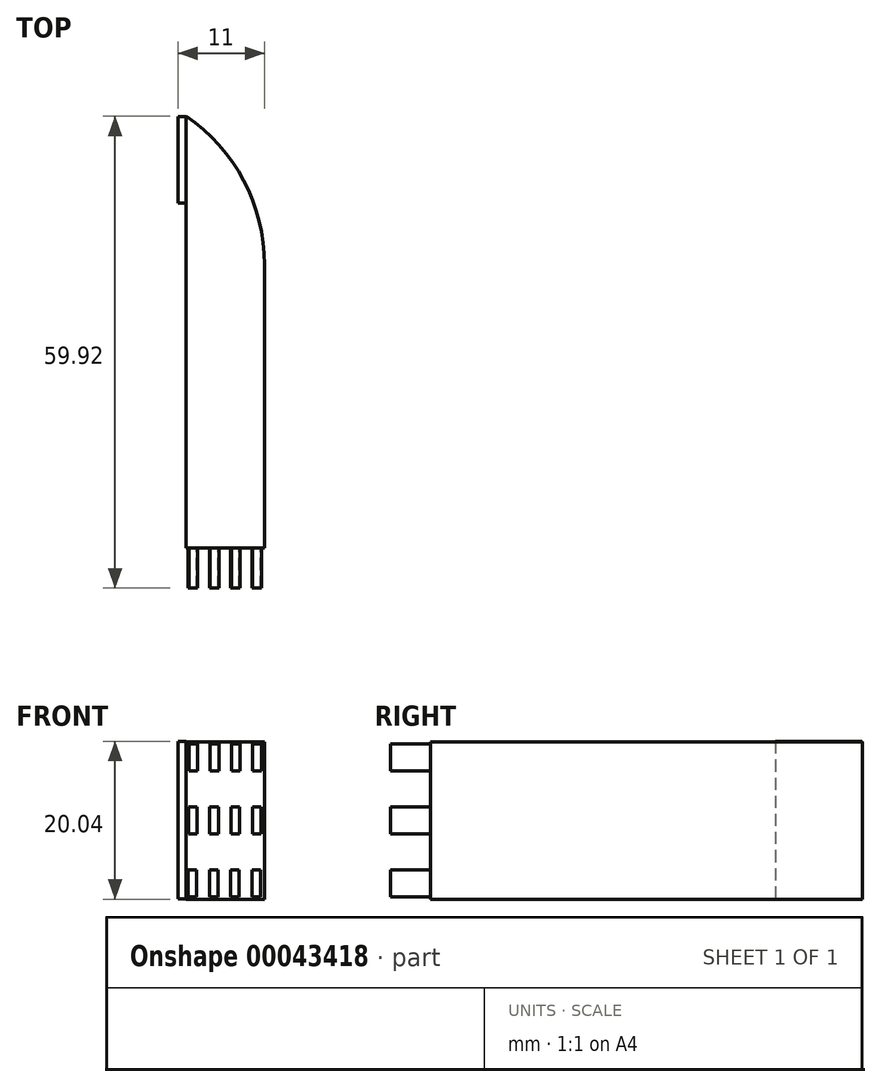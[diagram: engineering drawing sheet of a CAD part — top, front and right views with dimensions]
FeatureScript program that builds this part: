
annotation { "Feature Type Name" : "Feature", "Feature Type Description" : "" }
export const myFeature = defineFeature(function(context is Context, id is Id, definition is map)
    precondition{}
    {
        {
            var Q0;
            Q0=qCreatedBy(makeId("Front.planeOp"),FACE);
            var sketch = newSketch(context, id + "F0", { "sketchPlane" : qUnion([Q0])});
            skLineSegment(sketch, "E0.rect.bottom", {"start": v(-5, 10) * mm, "end": v(5, 10) * mm});
            skLineSegment(sketch, "E0.rect.top", {"start": v(-5, -10) * mm, "end": v(5, -10) * mm});
            skLineSegment(sketch, "E0.rect.left", {"start": v(-5, 10) * mm, "end": v(-5, -10) * mm});
            skLineSegment(sketch, "E0.rect.right", {"start": v(5, 10) * mm, "end": v(5, -10) * mm});
            skPoint(sketch, "E0.rect.middle", {"position": v(0, 0) * mm});
            skSolve(sketch);
        }
        {
            var Q0;
            Q0=qSketchRegion(id+"F0",true);
            extrude(context, id + "F1", {"entities" : qUnion([Q0]), "oppositeDirection" : true, "depth" : 25 * mm});
        }
        {
            var Q0;
            Q0=makeQuery(id+"F1.opExtrude","CAP_EDGE",EDGE,{"disambiguationData":[OSD([sQuery(id+"F0.wireOp",EDGE,"E0.rect.left")])],"isStart":false});
            cPlane(context, id + "F2", {"entities" : qUnion([Q0]), "cplaneType" : CPlaneType.LINE_ANGLE, "offset" : 150 * mm, "angle" : 0 * degree, "width" : 150 * mm, "height" : 150 * mm});
        }
        {
            var Q0;
            Q0=qCreatedBy(id+"F2.planeOp",FACE);
            var sketch = newSketch(context, id + "F3", { "sketchPlane" : qUnion([Q0])});
            skLineSegment(sketch, "E1.rect.bottom", {"start": v(-54.87, 10) * mm, "end": v(-24.87, 10) * mm});
            skLineSegment(sketch, "E1.rect.top", {"start": v(-54.87, -10) * mm, "end": v(-24.87, -10) * mm});
            skLineSegment(sketch, "E1.rect.left", {"start": v(-54.87, 10) * mm, "end": v(-54.87, -10) * mm});
            skLineSegment(sketch, "E1.rect.right", {"start": v(-24.87, 10) * mm, "end": v(-24.87, -10) * mm});
            skPoint(sketch, "E1.rect.middle", {"position": v(-39.87, 0) * mm});
            skSolve(sketch);
        }
        {
            var Q0;
            Q0=makeQuery(id+"F3.imprint","IMPRINT",FACE,{"disambiguationData":[TD([[makeQuery(id+"F3.imprint","IMPRINT",EDGE,{"derivedFrom":sQuery(id+"F3.wireOp",EDGE,"E1.rect.bottom")}),-1.0]])]});
            extrude(context, id + "F4", {"entities" : qUnion([Q0]), "operationType" : NewBodyOperationType.ADD, "oppositeDirection" : true, "depth" : 10 * mm});
        }
        {
            var Q0;
            Q0=makeQuery(id+"F4.opExtrude","CAP_EDGE",EDGE,{"disambiguationData":[OSD([sQuery(id+"F3.wireOp",EDGE,"E1.rect.left")])],"isStart":false});
            fillet(context, id + "F5", {"entities" : qUnion([Q0]), "radius" : 22.72 * mm, "tangentPropagation" : true, "allowEdgeOverflow" : false});
        }
        {
            var Q0;
            Q0=qCreatedBy(id+"F2.planeOp",FACE);
            var sketch = newSketch(context, id + "F6", { "sketchPlane" : qUnion([Q0])});
            skLineSegment(sketch, "E2.bottom", {"start": v(-54.82, 10.04) * mm, "end": v(-43.82, 10.04) * mm});
            skLineSegment(sketch, "E2.top", {"start": v(-54.82, -9.96) * mm, "end": v(-43.82, -9.96) * mm});
            skLineSegment(sketch, "E2.left", {"start": v(-54.82, 10.04) * mm, "end": v(-54.82, -9.96) * mm});
            skLineSegment(sketch, "E2.right", {"start": v(-43.82, 10.04) * mm, "end": v(-43.82, -9.96) * mm});
            skSolve(sketch);
        }
        {
            var Q0;
            Q0=makeQuery(id+"F6.imprint","IMPRINT",FACE,{"disambiguationData":[TD([[makeQuery(id+"F6.imprint","IMPRINT",EDGE,{"derivedFrom":sQuery(id+"F6.wireOp",EDGE,"E2.bottom")}),-1.0]])]});
            extrude(context, id + "F7", {"entities" : qUnion([Q0]), "operationType" : NewBodyOperationType.ADD, "depth" : 1 * mm});
        }
        {
            var Q0;
            Q0=makeQuery(id+"F1.opExtrude","CAP_FACE",FACE,{"disambiguationData":[OSD([sQuery(id+"F0.wireOp",EDGE,"E0.rect.bottom"),sQuery(id+"F0.wireOp",EDGE,"E0.rect.top"),sQuery(id+"F0.wireOp",EDGE,"E0.rect.left"),sQuery(id+"F0.wireOp",EDGE,"E0.rect.right")])],"isStart":true});
            var sketch = newSketch(context, id + "F8", { "sketchPlane" : qUnion([Q0])});
            skLineSegment(sketch, "E3.bottom", {"start": v(-4.6, 9.7) * mm, "end": v(-3.5, 9.7) * mm});
            skLineSegment(sketch, "E3.top", {"start": v(-4.6, 6.3) * mm, "end": v(-3.5, 6.3) * mm});
            skLineSegment(sketch, "E3.left", {"start": v(-4.6, 9.7) * mm, "end": v(-4.6, 6.3) * mm});
            skLineSegment(sketch, "E3.right", {"start": v(-3.5, 9.7) * mm, "end": v(-3.5, 6.3) * mm});
            skLineSegment(sketch, "E4.1.0.0", {"start": v(-0.8, 9.7) * mm, "end": v(-0.8, 6.3) * mm});
            skLineSegment(sketch, "E4.1.0.1", {"start": v(-1.9, 9.7) * mm, "end": v(-0.8, 9.7) * mm});
            skLineSegment(sketch, "E4.1.0.2", {"start": v(-1.9, 9.7) * mm, "end": v(-1.9, 6.3) * mm});
            skLineSegment(sketch, "E4.1.0.3", {"start": v(-1.9, 6.3) * mm, "end": v(-0.8, 6.3) * mm});
            skLineSegment(sketch, "E4.2.0.0", {"start": v(1.9, 9.7) * mm, "end": v(1.9, 6.3) * mm});
            skLineSegment(sketch, "E4.2.0.1", {"start": v(0.8, 9.7) * mm, "end": v(1.9, 9.7) * mm});
            skLineSegment(sketch, "E4.2.0.2", {"start": v(0.8, 9.7) * mm, "end": v(0.8, 6.3) * mm});
            skLineSegment(sketch, "E4.2.0.3", {"start": v(0.8, 6.3) * mm, "end": v(1.9, 6.3) * mm});
            skLineSegment(sketch, "E4.3.0.0", {"start": v(4.6, 9.7) * mm, "end": v(4.6, 6.3) * mm});
            skLineSegment(sketch, "E4.3.0.1", {"start": v(3.5, 9.7) * mm, "end": v(4.6, 9.7) * mm});
            skLineSegment(sketch, "E4.3.0.2", {"start": v(3.5, 9.7) * mm, "end": v(3.5, 6.3) * mm});
            skLineSegment(sketch, "E4.3.0.3", {"start": v(3.5, 6.3) * mm, "end": v(4.6, 6.3) * mm});
            skLineSegment(sketch, "E4.direction1", {"start": v(-3.5, 6.3) * mm, "end": v(-0.8, 6.3) * mm, "construction": true});
            skLineSegment(sketch, "E5.1.0.0", {"start": v(-4.66, -1.7) * mm, "end": v(-3.56, -1.7) * mm});
            skLineSegment(sketch, "E5.1.0.1", {"start": v(-4.66, 1.7) * mm, "end": v(-4.66, -1.7) * mm});
            skLineSegment(sketch, "E5.1.0.2", {"start": v(-3.56, 1.7) * mm, "end": v(-3.56, -1.7) * mm});
            skLineSegment(sketch, "E5.1.0.3", {"start": v(-4.66, 1.7) * mm, "end": v(-3.56, 1.7) * mm});
            skLineSegment(sketch, "E5.2.0.0", {"start": v(-4.72, -9.7) * mm, "end": v(-3.62, -9.7) * mm});
            skLineSegment(sketch, "E5.2.0.1", {"start": v(-4.72, -6.3) * mm, "end": v(-4.72, -9.7) * mm});
            skLineSegment(sketch, "E5.2.0.2", {"start": v(-3.62, -6.3) * mm, "end": v(-3.62, -9.7) * mm});
            skLineSegment(sketch, "E5.2.0.3", {"start": v(-4.72, -6.3) * mm, "end": v(-3.62, -6.3) * mm});
            skLineSegment(sketch, "E5.direction1", {"start": v(-4.6, 6.3) * mm, "end": v(-4.66, -1.7) * mm, "construction": true});
            skLineSegment(sketch, "E6.1.0.0", {"start": v(-1.96, 1.7) * mm, "end": v(-1.96, -1.7) * mm});
            skLineSegment(sketch, "E6.1.0.1", {"start": v(-1.96, -1.7) * mm, "end": v(-0.86, -1.7) * mm});
            skLineSegment(sketch, "E6.1.0.2", {"start": v(-0.86, 1.7) * mm, "end": v(-0.86, -1.7) * mm});
            skLineSegment(sketch, "E6.1.0.3", {"start": v(-1.96, 1.7) * mm, "end": v(-0.86, 1.7) * mm});
            skLineSegment(sketch, "E6.2.0.0", {"start": v(-2.02, -6.3) * mm, "end": v(-2.02, -9.7) * mm});
            skLineSegment(sketch, "E6.2.0.1", {"start": v(-2.02, -9.7) * mm, "end": v(-0.92, -9.7) * mm});
            skLineSegment(sketch, "E6.2.0.2", {"start": v(-0.92, -6.3) * mm, "end": v(-0.92, -9.7) * mm});
            skLineSegment(sketch, "E6.2.0.3", {"start": v(-2.02, -6.3) * mm, "end": v(-0.92, -6.3) * mm});
            skLineSegment(sketch, "E6.direction1", {"start": v(-1.9, 6.3) * mm, "end": v(-1.96, -1.7) * mm, "construction": true});
            skLineSegment(sketch, "E7.1.0.0", {"start": v(1.84, 1.7) * mm, "end": v(1.84, -1.7) * mm});
            skLineSegment(sketch, "E7.1.0.1", {"start": v(0.74, 1.7) * mm, "end": v(0.74, -1.7) * mm});
            skLineSegment(sketch, "E7.1.0.2", {"start": v(0.74, 1.7) * mm, "end": v(1.84, 1.7) * mm});
            skLineSegment(sketch, "E7.1.0.3", {"start": v(0.74, -1.7) * mm, "end": v(1.84, -1.7) * mm});
            skLineSegment(sketch, "E7.2.0.0", {"start": v(1.78, -6.3) * mm, "end": v(1.78, -9.7) * mm});
            skLineSegment(sketch, "E7.2.0.1", {"start": v(0.68, -6.3) * mm, "end": v(0.68, -9.7) * mm});
            skLineSegment(sketch, "E7.2.0.2", {"start": v(0.68, -6.3) * mm, "end": v(1.78, -6.3) * mm});
            skLineSegment(sketch, "E7.2.0.3", {"start": v(0.68, -9.7) * mm, "end": v(1.78, -9.7) * mm});
            skLineSegment(sketch, "E7.direction1", {"start": v(1.9, 6.3) * mm, "end": v(1.84, -1.7) * mm, "construction": true});
            skLineSegment(sketch, "E8.1.0.0", {"start": v(3.44, 1.7) * mm, "end": v(3.44, -1.7) * mm});
            skLineSegment(sketch, "E8.1.0.1", {"start": v(3.44, -1.7) * mm, "end": v(4.54, -1.7) * mm});
            skLineSegment(sketch, "E8.1.0.2", {"start": v(4.54, 1.7) * mm, "end": v(4.54, -1.7) * mm});
            skLineSegment(sketch, "E8.1.0.3", {"start": v(3.44, 1.7) * mm, "end": v(4.54, 1.7) * mm});
            skLineSegment(sketch, "E8.2.0.0", {"start": v(3.38, -6.3) * mm, "end": v(3.38, -9.7) * mm});
            skLineSegment(sketch, "E8.2.0.1", {"start": v(3.38, -9.7) * mm, "end": v(4.48, -9.7) * mm});
            skLineSegment(sketch, "E8.2.0.2", {"start": v(4.48, -6.3) * mm, "end": v(4.48, -9.7) * mm});
            skLineSegment(sketch, "E8.2.0.3", {"start": v(3.38, -6.3) * mm, "end": v(4.48, -6.3) * mm});
            skLineSegment(sketch, "E8.direction1", {"start": v(3.5, 6.3) * mm, "end": v(3.44, -1.7) * mm, "construction": true});
            skSolve(sketch);
        }
        {
            var Q0;
            Q0=qSketchRegion(id+"F8",true);
            extrude(context, id + "F9", {"entities" : qUnion([Q0]), "operationType" : NewBodyOperationType.ADD, "depth" : 5.05 * mm});
        }
    });
